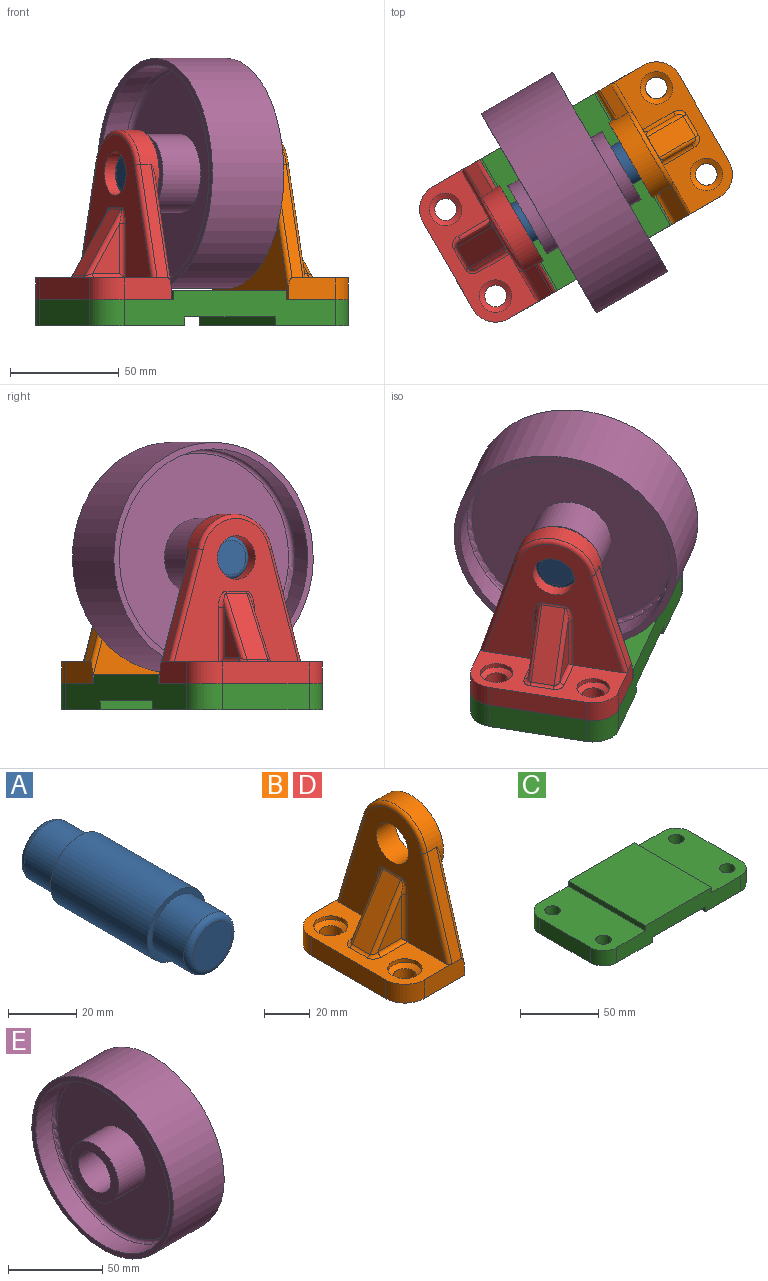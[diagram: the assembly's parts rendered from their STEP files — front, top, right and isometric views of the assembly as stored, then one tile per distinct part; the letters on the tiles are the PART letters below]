
ASSEMBLY  parts=5 mates=6
PART A: 9 faces, bbox 24x70x24 mm
  f0: cylinder r=12mm len=40mm, axis (0,1,0), area 3015.9mm2, adj f2,f5
  f1: cylinder r=10mm len=20mm, axis (0,-1,0), area 816.8mm2, adj f2,f8
  f2: plane 24x24mm, normal (0,-1,0), area 138.2mm2, adj f0,f1
  f3: plane 16x16mm, normal (0,-1,0), area 201.1mm2, adj f8
  f4: cylinder r=10mm len=20mm, axis (0,1,0), area 816.8mm2, adj f5,f7
  f5: plane 24x24mm, normal (0,1,0), area 138.2mm2, adj f0,f4
  f6: plane 16x16mm, normal (0,1,0), area 201.1mm2, adj f7
  f7: torus R=8mm, axis (0,-1,0), area 183mm2, adj f4,f6
  f8: torus R=8mm, axis (0,-1,0), area 183mm2, adj f1,f3
PART B: 40 faces, bbox 39x73.8x79.6 mm
  f0: plane 23.03x14.39mm, normal (0,-1,0), area 165.7mm2, adj f23,f24,f25
  f1: plane 66x65.83mm, normal (-1,0,0), area 2068.5mm2, adj f2,f16,f23,f26,f28,f29,f32,f37
  f2: plane 70x29.22mm, normal (0,0,1), area 1098.6mm2, adj f1,f3,f4,f8,f10,f11,f12,f14
  f3: plane 25x10mm, normal (0,1,0), area 247mm2, adj f2,f5,f9,f10,f19,f35
  f4: plane 25x10mm, normal (0,-1,0), area 247mm2, adj f2,f5,f9,f11,f18,f36
  f5: plane 70x54.6mm, normal (1,0,0), area 2539.3mm2, adj f3,f4,f9,f17,f35,f36
  f6: cylinder r=5mm len=10mm, axis (0,0,1), area 204.1mm2, adj f9,f15
  f7: cylinder r=5mm len=10mm, axis (0,0,1), area 204.1mm2, adj f9,f13
  f8: plane 46x10mm, normal (-1,0,0), area 460mm2, adj f2,f9,f10,f11
  f9: plane 70x37mm, normal (0,0,-1), area 2371.1mm2, adj f3,f4,f5,f6,f7,f8,f10,f11
  f10: cylinder r=12mm len=12mm, axis (0,0,-1), area 188.5mm2, adj f2,f3,f8,f9
  f11: cylinder r=12mm len=12mm, axis (0,0,1), area 188.5mm2, adj f2,f4,f8,f9
  f12: cylinder r=7.5mm len=15mm, axis (0,0,1), area 94.2mm2, adj f2,f13
  f13: cone r=0mm half-angle=59deg, axis (0,0,1), area 114.5mm2, adj f7,f12
  f14: cylinder r=7.5mm len=15mm, axis (0,0,1), area 94.2mm2, adj f2,f15
  f15: cone r=0mm half-angle=59deg, axis (0,0,1), area 114.5mm2, adj f6,f14
  f16: cylinder r=10mm len=20mm, axis (-1,0,0), area 740.5mm2, adj f1,f20
  f17: cylinder r=20mm len=40mm, axis (-1,0,0), area 686.1mm2, adj f5,f18,f19,f20,f35,f36,f38
  f18: plane 52.08x15.42mm, normal (0,-0.96,0.28), area 314.2mm2, adj f4,f17,f36,f37
  f19: plane 52.08x15.42mm, normal (0,0.96,0.28), area 314.2mm2, adj f3,f17,f35,f39
  f20: plane 40x40mm, normal (1,0,0), area 942.5mm2, adj f16,f17
  f21: plane 23.03x14.39mm, normal (0,1,0), area 165.7mm2, adj f28,f31,f34
  f22: plane 30.57x19.11mm, normal (-0.85,0,0.53), area 396.6mm2, adj f24,f29,f30,f34
  f23: cylinder r=2mm len=25.03mm, axis (0,0,1), area 76.3mm2, adj f0,f1,f25,f26
  f24: cylinder r=2mm len=31.63mm, axis (0.53,0,0.85), area 103.1mm2, adj f0,f22,f26,f27
  f25: cylinder r=2mm len=16.39mm, axis (1,0,0), area 49.2mm2, adj f0,f2,f23,f27
  f26: bspline ~7.55x4mm, area 17mm2, adj f1,f23,f24,f29
  f27: bspline ~4.72x4mm, area 12.8mm2, adj f2,f24,f25,f30
  f28: cylinder r=2mm len=25.03mm, axis (0,0,-1), area 76.3mm2, adj f1,f21,f31,f32
  f29: cylinder r=2mm len=11mm, axis (0,1,0), area 12.3mm2, adj f1,f22,f26,f32
  f30: cylinder r=2mm len=11mm, axis (0,-1,0), area 22.3mm2, adj f2,f22,f27,f33
  f31: cylinder r=2mm len=16.39mm, axis (-1,0,0), area 49.2mm2, adj f2,f21,f28,f33
  f32: bspline ~7.55x4mm, area 17mm2, adj f1,f28,f29,f34
  f33: bspline ~4.72x4mm, area 12.8mm2, adj f2,f30,f31,f34
  f34: cylinder r=2mm len=31.63mm, axis (0.53,0,0.85), area 103.1mm2, adj f21,f22,f32,f33
  f35: cylinder r=2mm len=59.12mm, axis (0,-0.28,0.96), area 167.6mm2, adj f3,f5,f17,f19
  f36: cylinder r=2mm len=59.12mm, axis (0,-0.28,-0.96), area 167.6mm2, adj f4,f5,f17,f18
  f37: cylinder r=2mm len=52.73mm, axis (0,-0.28,-0.96), area 170.1mm2, adj f1,f2,f18,f38
  f38: torus R=18mm, axis (1,0,0), area 165.6mm2, adj f1,f17,f37,f39
  f39: cylinder r=2mm len=52.73mm, axis (0,-0.28,0.96), area 170.1mm2, adj f1,f2,f19,f38
PART C: 22 faces, bbox 136x70x16 mm
  f0: plane 70x60mm, normal (0,0,1), area 4200mm2, adj f1,f11,f12,f13
  f1: plane 70x4mm, normal (-1,0,0), area 280mm2, adj f0,f2,f12,f13
  f2: plane 70x38mm, normal (0,0,1), area 2441.1mm2, adj f1,f3,f12,f13,f15,f17,f18,f19
  f3: plane 46x12mm, normal (-1,0,0), area 552mm2, adj f2,f4,f15,f17
  f4: plane 70x44mm, normal (0,0,-1), area 2861.1mm2, adj f3,f5,f12,f13,f15,f17,f18,f19
  f5: plane 70x4mm, normal (1,0,0), area 280mm2, adj f4,f6,f12,f13
  f6: plane 70x48mm, normal (0,0,-1), area 3360mm2, adj f5,f7,f12,f13
  f7: plane 70x4mm, normal (-1,0,0), area 280mm2, adj f6,f8,f12,f13
  f8: plane 70x44mm, normal (0,0,-1), area 2861.1mm2, adj f7,f9,f12,f13,f14,f16,f20,f21
  f9: plane 46x12mm, normal (1,0,0), area 552mm2, adj f8,f10,f14,f16
  f10: plane 70x38mm, normal (0,0,1), area 2441.1mm2, adj f9,f11,f12,f13,f14,f16,f20,f21
  f11: plane 70x4mm, normal (1,0,0), area 280mm2, adj f0,f10,f12,f13
  f12: plane 112x16mm, normal (0,-1,0), area 1392mm2, adj f0,f1,f2,f4,f5,f6,f7,f8
  f13: plane 112x16mm, normal (0,1,0), area 1392mm2, adj f0,f1,f2,f4,f5,f6,f7,f8
  f14: cylinder r=12mm len=12mm, axis (0,0,1), area 226.2mm2, adj f8,f9,f10,f13
  f15: cylinder r=12mm len=12mm, axis (0,0,-1), area 226.2mm2, adj f2,f3,f4,f13
  f16: cylinder r=12mm len=12mm, axis (0,0,-1), area 226.2mm2, adj f8,f9,f10,f12
  f17: cylinder r=12mm len=12mm, axis (0,0,1), area 226.2mm2, adj f2,f3,f4,f12
  f18: cylinder r=5mm len=12mm, axis (0,0,1), area 377mm2, adj f2,f4
  f19: cylinder r=5mm len=12mm, axis (0,0,1), area 377mm2, adj f2,f4
  f20: cylinder r=5mm len=12mm, axis (0,0,1), area 377mm2, adj f8,f10
  f21: cylinder r=5mm len=12mm, axis (0,0,1), area 377mm2, adj f8,f10
PART D: same geometry as B
PART E: 14 faces, bbox 50x108.2x108.2 mm
  f0: cylinder r=53mm len=106mm, axis (-1,0,0), area 12654.3mm2, adj f1,f11
  f1: plane 106x106mm, normal (-1,0,0), area 970.8mm2, adj f0,f2
  f2: cylinder r=50mm len=100mm, axis (-1,0,0), area 3769.9mm2, adj f1,f12
  f3: plane 96x96mm, normal (-1,0,0), area 6220.4mm2, adj f4,f12
  f4: cylinder r=18mm len=36mm, axis (-1,0,0), area 2261.9mm2, adj f3,f5
  f5: plane 36x36mm, normal (-1,0,0), area 565.5mm2, adj f4,f6
  f6: cylinder r=12mm len=50mm, axis (-1,0,0), area 3769.9mm2, adj f5,f7
  f7: plane 36x36mm, normal (1,0,0), area 565.5mm2, adj f6,f8
  f8: cylinder r=18mm len=36mm, axis (-1,0,0), area 2261.9mm2, adj f7,f9
  f9: plane 96x96mm, normal (1,0,0), area 6220.4mm2, adj f8,f13
  f10: cylinder r=50mm len=100mm, axis (-1,0,0), area 3769.9mm2, adj f11,f13
  f11: plane 106x106mm, normal (1,0,0), area 970.8mm2, adj f0,f10
  f12: torus R=48mm, axis (1,0,0), area 972.6mm2, adj f2,f3
  f13: torus R=48mm, axis (1,0,0), area 972.6mm2, adj f9,f10
PLACE A rot(axis=(-0.45,-0.77,-0.45),104.5deg) t=(-87.19,100.04,30.57)mm
PLACE B rot(axis=(0,0,-1),150deg) t=(-27.61,134.44,-17.43)mm
PLACE C rot(axis=(0,0,1),30deg) t=(-145.39,66.44,-27.43)mm
PLACE D rot(axis=(0,0,1),30deg) t=(-145.39,66.44,-17.43)mm
PLACE E rot(axis=(0,0,1),30deg) t=(-103.65,90.54,83.57)mm
MATE slider D.f6 <-> C.f15  axis (0,0,1) through (-146.5,92.36,-19.43)mm
MATE slider A.f1 <-> D.f16  axis (-0.87,-0.5,0) through (-110.14,86.79,30.57)mm
MATE fastened B.f6 <-> C.f16  axis (0,0,-1) through (-26.5,108.52,-27.43)mm
MATE slider B.f6 <-> C.f16  axis (0,0,-1) through (-26.5,108.52,-27.43)mm
MATE revolute E.f0 <-> A.f0  axis (-0.87,-0.5,0) through (-87.19,100.04,30.57)mm
MATE fastened D.f7 <-> C.f17  axis (0,0,-1) through (-123.5,52.52,-27.43)mm
